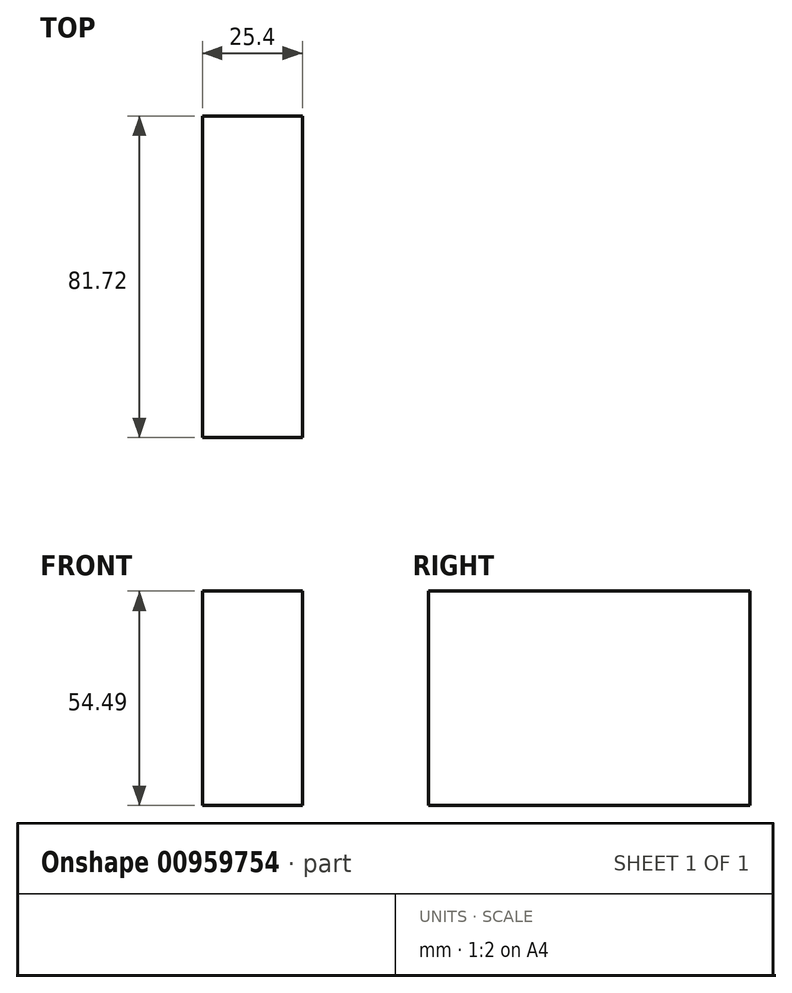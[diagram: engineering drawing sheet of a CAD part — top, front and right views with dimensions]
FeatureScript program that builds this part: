
annotation { "Feature Type Name" : "Feature", "Feature Type Description" : "" }
export const myFeature = defineFeature(function(context is Context, id is Id, definition is map)
    precondition{}
    {
        {
            var Q0;
            Q0=qCreatedBy(makeId("Right.planeOp"),FACE);
            var sketch = newSketch(context, id + "F0", { "sketchPlane" : qUnion([Q0])});
            skLineSegment(sketch, "E0.bottom", {"start": v(-24.52, 14) * mm, "end": v(57.2, 14) * mm});
            skLineSegment(sketch, "E0.top", {"start": v(-24.52, -40.48) * mm, "end": v(57.2, -40.48) * mm});
            skLineSegment(sketch, "E0.left", {"start": v(-24.52, 14) * mm, "end": v(-24.52, -40.48) * mm});
            skLineSegment(sketch, "E0.right", {"start": v(57.2, 14) * mm, "end": v(57.2, -40.48) * mm});
            skSolve(sketch);
        }
        {
            var Q0;
            Q0 = qSketchRegion(id + "F0", true);
            extrude(context, id + "F1", {"entities" : qUnion([Q0]), "depth" : 25.4 * mm, "offsetDistance" : 25.4 * mm});
        }
    });
